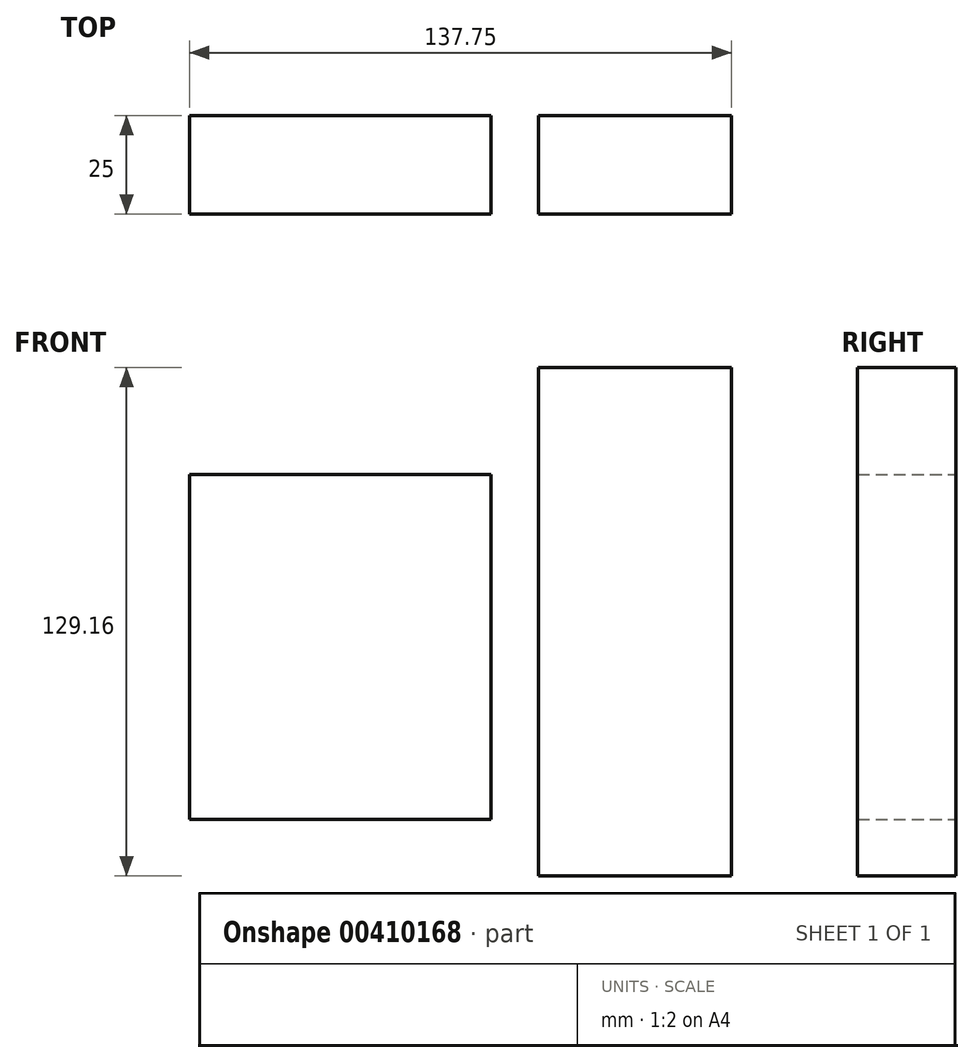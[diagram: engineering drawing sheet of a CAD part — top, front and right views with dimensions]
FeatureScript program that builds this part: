
annotation { "Feature Type Name" : "Feature", "Feature Type Description" : "" }
export const myFeature = defineFeature(function(context is Context, id is Id, definition is map)
    precondition{}
    {
        {
            var Q0;
            Q0=qCreatedBy(makeId("Front.planeOp"),FACE);
            var sketch = newSketch(context, id + "F0", { "sketchPlane" : qUnion([Q0])});
            skLineSegment(sketch, "E0.bottom", {"start": v(85.44, 24.82) * mm, "end": v(8.86, 24.82) * mm});
            skLineSegment(sketch, "E0.top", {"start": v(85.44, 112.44) * mm, "end": v(8.86, 112.44) * mm});
            skLineSegment(sketch, "E0.left", {"start": v(85.44, 24.82) * mm, "end": v(85.44, 112.44) * mm});
            skLineSegment(sketch, "E0.right", {"start": v(8.86, 24.82) * mm, "end": v(8.86, 112.44) * mm});
            skLineSegment(sketch, "E1.bottom", {"start": v(97.52, 10.5) * mm, "end": v(146.6, 10.5) * mm});
            skLineSegment(sketch, "E1.top", {"start": v(97.52, 139.67) * mm, "end": v(146.6, 139.67) * mm});
            skLineSegment(sketch, "E1.left", {"start": v(97.52, 10.5) * mm, "end": v(97.52, 139.67) * mm});
            skLineSegment(sketch, "E1.right", {"start": v(146.6, 10.5) * mm, "end": v(146.6, 139.67) * mm});
            skSolve(sketch);
        }
        {
            var Q0;
            Q0=makeQuery(id+"F0.imprint","IMPRINT",FACE,{"disambiguationData":[TD([[makeQuery(id+"F0.imprint","IMPRINT",EDGE,{"derivedFrom":sQuery(id+"F0.wireOp",EDGE,"E0.bottom")}),-1.0]])]});
            var Q1;
            Q1=makeQuery(id+"F0.imprint","IMPRINT",FACE,{"disambiguationData":[TD([[makeQuery(id+"F0.imprint","IMPRINT",EDGE,{"derivedFrom":sQuery(id+"F0.wireOp",EDGE,"E1.bottom")}),1.0]])]});
            extrude(context, id + "F1", {"entities" : qUnion([Q0, Q1]), "depth" : 25 * mm});
        }
    });
